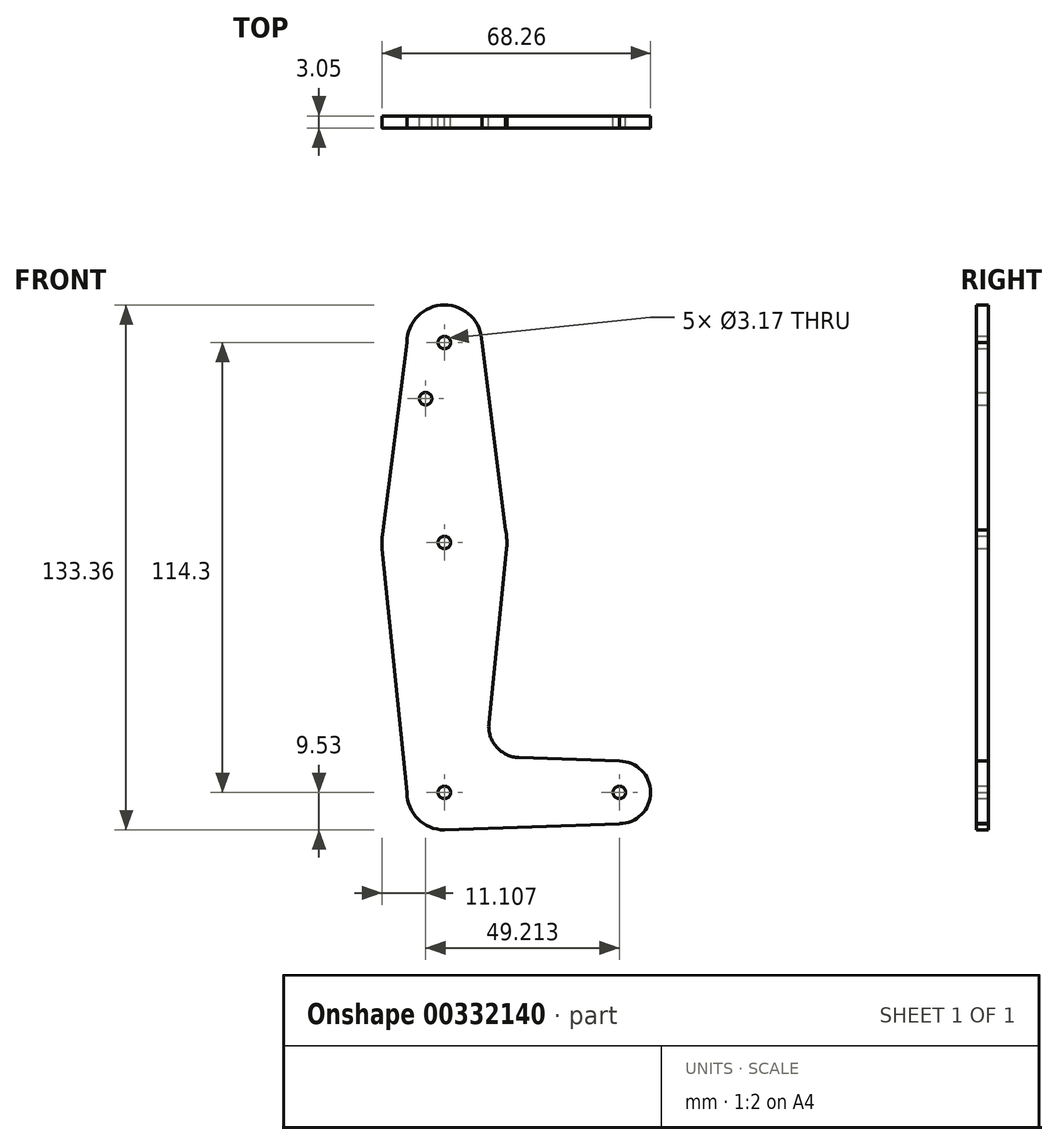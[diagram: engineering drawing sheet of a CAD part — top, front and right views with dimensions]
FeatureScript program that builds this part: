
annotation { "Feature Type Name" : "Feature", "Feature Type Description" : "" }
export const myFeature = defineFeature(function(context is Context, id is Id, definition is map)
    precondition{}
    {
        {
            var Q0;
            Q0=qCreatedBy(makeId("Front.planeOp"),FACE);
            var sketch = newSketch(context, id + "F0", { "sketchPlane" : qUnion([Q0])});
            skLineSegment(sketch, "E0", {"start": v(0, 0) * mm, "end": v(0, 114.3) * mm});
            skLineSegment(sketch, "E1", {"start": v(0, 0) * mm, "end": v(44.45, 0) * mm});
            skCircle(sketch, "E2", {"center": v(0, 114.3) * mm, "radius": 9.53 * mm});
            skCircle(sketch, "E3", {"center": v(0, 0) * mm, "radius": 9.53 * mm});
            skCircle(sketch, "E4", {"center": v(44.45, 0) * mm, "radius": 7.94 * mm});
            skLineSegment(sketch, "E5", {"start": v(0, 114.3) * mm, "end": v(-9.53, 114.3) * mm});
            skLineSegment(sketch, "E6", {"start": v(-9.53, 0) * mm, "end": v(9.53, 0) * mm});
            skLineSegment(sketch, "E7", {"start": v(9.6, 114.3) * mm, "end": v(9.53, 114.3) * mm});
            skPoint(sketch, "E8.center.orphan", {"position": v(0, 63.5) * mm});
            skCircle(sketch, "E9", {"center": v(0, 63.5) * mm, "radius": 15.88 * mm});
            skLineSegment(sketch, "E10", {"start": v(-9.53, 114.3) * mm, "end": v(-15.75, 65.5) * mm});
            skLineSegment(sketch, "E11", {"start": v(-9.53, 0) * mm, "end": v(-15.8, 61.9) * mm});
            skLineSegment(sketch, "E12", {"start": v(11.3, 17.6) * mm, "end": v(15.8, 61.9) * mm});
            skLineSegment(sketch, "E13", {"start": v(0, 114.3) * mm, "end": v(9.6, 114.3) * mm});
            skLineSegment(sketch, "E14", {"start": v(9.6, 114.3) * mm, "end": v(15.7, 65.5) * mm});
            skCircle(sketch, "E15", {"center": v(0, 63.5) * mm, "radius": 1.59 * mm});
            skCircle(sketch, "E16", {"center": v(0, 114.3) * mm, "radius": 1.59 * mm});
            skCircle(sketch, "E17", {"center": v(0, 0) * mm, "radius": 1.59 * mm});
            skCircle(sketch, "E18", {"center": v(44.45, 0) * mm, "radius": 1.59 * mm});
            skCircle(sketch, "E19", {"center": v(-4.76, 100.03) * mm, "radius": 1.59 * mm});
            skLineSegment(sketch, "E20", {"start": v(0, -9.53) * mm, "end": v(44.45, -7.94) * mm});
            skLineSegment(sketch, "E21", {"start": v(18.93, 8.85) * mm, "end": v(44.45, 7.94) * mm});
            skPoint(sketch, "E22.newPointB", {"position": v(0, 9.52) * mm});
            skArc(sketch, "E22.filletArc", {"start": v(11.3, 17.6) * mm, "mid": v(13.22, 11.57) * mm, "end": v(18.93, 8.85) * mm});
            skLineSegment(sketch, "E23", {"start": v(0, -1.59) * mm, "end": v(0, -9.53) * mm});
            skLineSegment(sketch, "E24", {"start": v(44.45, 0) * mm, "end": v(44.45, -7.94) * mm});
            skSolve(sketch);
        }
        {
            var Q0;
            {var subQ0=sQuery(id+"F0.wireOp",EDGE,"E2");var subQ1=sQuery(id+"F0.wireOp",EDGE,"E0");var subQ2=makeQuery(id+"F0.imprint","INTERSECT",VERTEX,{"derivedFrom":[subQ1,subQ0]});Q0=makeQuery(id+"F0.imprint","IMPRINT",FACE,{"disambiguationData":[TD([[makeQuery(id+"F0.imprint","IMPRINT",EDGE,{"disambiguationData":[TD([[subQ2,-1.0]])],"derivedFrom":subQ1}),-1.0]])]});}
            var Q1;
            {var subQ0=sQuery(id+"F0.wireOp",EDGE,"E2");var subQ1=sQuery(id+"F0.wireOp",EDGE,"E0");var subQ2=makeQuery(id+"F0.imprint","INTERSECT",VERTEX,{"derivedFrom":[subQ1,subQ0]});Q1=makeQuery(id+"F0.imprint","IMPRINT",FACE,{"disambiguationData":[TD([[makeQuery(id+"F0.imprint","IMPRINT",EDGE,{"disambiguationData":[TD([[subQ2,-1.0]])],"derivedFrom":subQ1}),1.0]])]});}
            var Q2;
            {var subQ1=sQuery(id+"F0.wireOp",EDGE,"E2");var subQ3=sQuery(id+"F0.wireOp",EDGE,"E13");var subQ4=makeQuery(id+"F0.imprint","INTERSECT",VERTEX,{"derivedFrom":[subQ1,subQ3]});Q2=makeQuery(id+"F0.imprint","IMPRINT",FACE,{"disambiguationData":[TD([[makeQuery(id+"F0.imprint","IMPRINT",EDGE,{"disambiguationData":[TD([[subQ4,1.0]])],"derivedFrom":subQ3}),1.0]])]});}
            var Q3;
            {var subQ5=sQuery(id+"F0.wireOp",EDGE,"E9");var subQ7=sQuery(id+"F0.wireOp",EDGE,"E0");var subQ8=makeQuery(id+"F0.imprint","INTERSECT",VERTEX,{"disambiguationData":[OD(1.0)],"derivedFrom":[subQ7,subQ5]});Q3=makeQuery(id+"F0.imprint","IMPRINT",FACE,{"disambiguationData":[TD([[makeQuery(id+"F0.imprint","IMPRINT",EDGE,{"disambiguationData":[TD([[subQ8,-1.0]])],"derivedFrom":subQ7}),-1.0]])]});}
            var Q4;
            {var subQ0=sQuery(id+"F0.wireOp",EDGE,"E10");Q4=makeQuery(id+"F0.imprint","IMPRINT",FACE,{"disambiguationData":[TD([[makeQuery(id+"F0.imprint","IMPRINT",EDGE,{"derivedFrom":subQ0}),1.0]])]});}
            var Q5;
            {var subQ0=sQuery(id+"F0.wireOp",EDGE,"E9");var subQ4=sQuery(id+"F0.wireOp",EDGE,"E0");var subQ8=makeQuery(id+"F0.imprint","INTERSECT",VERTEX,{"disambiguationData":[OD(0.0)],"derivedFrom":[subQ4,subQ0]});Q5=makeQuery(id+"F0.imprint","IMPRINT",FACE,{"disambiguationData":[TD([[makeQuery(id+"F0.imprint","IMPRINT",EDGE,{"disambiguationData":[TD([[subQ8,-1.0]])],"derivedFrom":subQ4}),1.0]])]});}
            var Q6;
            {var subQ0=sQuery(id+"F0.wireOp",EDGE,"E9");var subQ2=sQuery(id+"F0.wireOp",EDGE,"E0");var subQ7=makeQuery(id+"F0.imprint","INTERSECT",VERTEX,{"disambiguationData":[OD(0.0)],"derivedFrom":[subQ2,subQ0]});Q6=makeQuery(id+"F0.imprint","IMPRINT",FACE,{"disambiguationData":[TD([[makeQuery(id+"F0.imprint","IMPRINT",EDGE,{"disambiguationData":[TD([[subQ7,-1.0]])],"derivedFrom":subQ2}),-1.0]])]});}
            var Q7;
            {var subQ8=sQuery(id+"F0.wireOp",EDGE,"E12");Q7=makeQuery(id+"F0.imprint","IMPRINT",FACE,{"disambiguationData":[TD([[makeQuery(id+"F0.imprint","IMPRINT",EDGE,{"derivedFrom":subQ8}),1.0]])]});}
            var Q8;
            {var subQ5=sQuery(id+"F0.wireOp",EDGE,"E11");Q8=makeQuery(id+"F0.imprint","IMPRINT",FACE,{"disambiguationData":[TD([[makeQuery(id+"F0.imprint","IMPRINT",EDGE,{"derivedFrom":subQ5}),-1.0]])]});}
            var Q9;
            {var subQ0=sQuery(id+"F0.wireOp",EDGE,"E17");var subQ1=sQuery(id+"F0.wireOp",EDGE,"E0");var subQ2=makeQuery(id+"F0.imprint","INTERSECT",VERTEX,{"derivedFrom":[subQ1,subQ0]});Q9=makeQuery(id+"F0.imprint","IMPRINT",FACE,{"disambiguationData":[TD([[makeQuery(id+"F0.imprint","IMPRINT",EDGE,{"disambiguationData":[TD([[subQ2,-1.0]])],"derivedFrom":subQ1}),-1.0]])]});}
            var Q10;
            {var subQ0=sQuery(id+"F0.wireOp",EDGE,"E17");var subQ1=sQuery(id+"F0.wireOp",EDGE,"E0");var subQ2=makeQuery(id+"F0.imprint","INTERSECT",VERTEX,{"derivedFrom":[subQ1,subQ0]});Q10=makeQuery(id+"F0.imprint","IMPRINT",FACE,{"disambiguationData":[TD([[makeQuery(id+"F0.imprint","IMPRINT",EDGE,{"disambiguationData":[TD([[subQ2,-1.0]])],"derivedFrom":subQ1}),1.0]])]});}
            var Q11;
            {var subQ3=sQuery(id+"F0.wireOp",EDGE,"E23");Q11=makeQuery(id+"F0.imprint","IMPRINT",FACE,{"disambiguationData":[TD([[makeQuery(id+"F0.imprint","IMPRINT",EDGE,{"derivedFrom":subQ3}),-1.0]])]});}
            var Q12;
            {var subQ0=sQuery(id+"F0.wireOp",EDGE,"E23");Q12=makeQuery(id+"F0.imprint","IMPRINT",FACE,{"disambiguationData":[TD([[makeQuery(id+"F0.imprint","IMPRINT",EDGE,{"derivedFrom":subQ0}),1.0]])]});}
            var Q13;
            {var subQ0=sQuery(id+"F0.wireOp",EDGE,"E24");var subQ5=sQuery(id+"F0.wireOp",EDGE,"E4");var subQ6=makeQuery(id+"F0.imprint","INTERSECT",VERTEX,{"derivedFrom":[subQ5,subQ0]});Q13=makeQuery(id+"F0.imprint","IMPRINT",FACE,{"disambiguationData":[TD([[makeQuery(id+"F0.imprint","IMPRINT",EDGE,{"disambiguationData":[TD([[subQ6,1.0]])],"derivedFrom":subQ5}),-1.0]])]});}
            var Q14;
            {var subQ0=sQuery(id+"F0.wireOp",EDGE,"E4");var subQ1=sQuery(id+"F0.wireOp",EDGE,"E1");var subQ2=makeQuery(id+"F0.imprint","INTERSECT",VERTEX,{"derivedFrom":[subQ1,subQ0]});Q14=makeQuery(id+"F0.imprint","IMPRINT",FACE,{"disambiguationData":[TD([[makeQuery(id+"F0.imprint","IMPRINT",EDGE,{"disambiguationData":[TD([[subQ2,-1.0]])],"derivedFrom":subQ1}),-1.0]])]});}
            var Q15;
            {var subQ1=sQuery(id+"F0.wireOp",EDGE,"E1");var subQ5=sQuery(id+"F0.wireOp",EDGE,"E4");var subQ8=makeQuery(id+"F0.imprint","INTERSECT",VERTEX,{"derivedFrom":[subQ1,subQ5]});Q15=makeQuery(id+"F0.imprint","IMPRINT",FACE,{"disambiguationData":[TD([[makeQuery(id+"F0.imprint","IMPRINT",EDGE,{"disambiguationData":[TD([[subQ8,-1.0]])],"derivedFrom":subQ1}),1.0]])]});}
            extrude(context, id + "F1", {"entities" : qUnion([Q0, Q1, Q2, Q3, Q4, Q5, Q6, Q7, Q8, Q9, Q10, Q11, Q12, Q13, Q14, Q15]), "depth" : 3.05 * mm});
        }
    });
